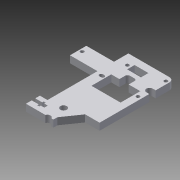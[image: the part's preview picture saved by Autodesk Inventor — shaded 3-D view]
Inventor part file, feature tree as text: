
AUTODESK INVENTOR PART (.ipt)
format: ipt  version: 2013 (Build 170138000, 138)  size: 143,360 bytes
history: native  units: mm
features: extrude x1, sketch x1
ambient origin geometry x8: Origin, YZ Plane, XZ Plane, XY Plane, X Axis, Y Axis, Z Axis, Center Point
bodies: Solid1 (feature_tree)
feature tree (2):
  extrude  "Extrusion1"  [1 undecoded]
  sketch  "Sketch1"  dims[d0=6.0mm d1=0.0mm]
note: 1 required parameter value undecoded (feature->parameter linkage not recoverable at this tier; creation-order binding heuristic only, values carry confidence <= 0.55)
